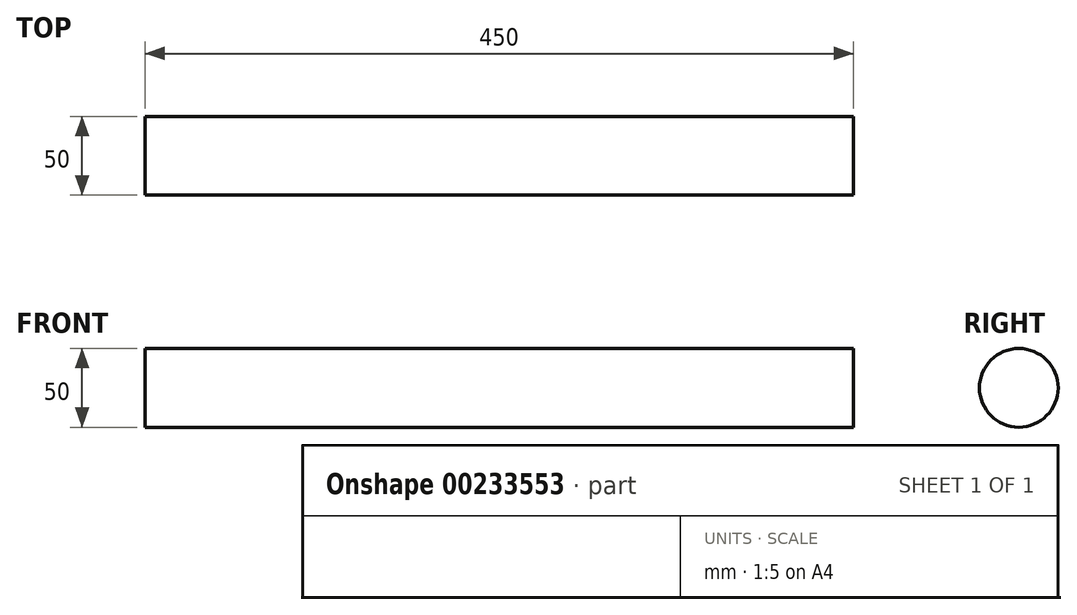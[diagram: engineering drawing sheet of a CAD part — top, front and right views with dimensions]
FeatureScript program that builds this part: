
annotation { "Feature Type Name" : "Feature", "Feature Type Description" : "" }
export const myFeature = defineFeature(function(context is Context, id is Id, definition is map)
    precondition{}
    {
        {
            var Q0;
            Q0=qCreatedBy(makeId("Front.planeOp"),FACE);
            var sketch = newSketch(context, id + "F0", { "sketchPlane" : qUnion([Q0])});
            skLineSegment(sketch, "E0.bottom", {"start": v(0, 0) * mm, "end": v(450, 0) * mm});
            skLineSegment(sketch, "E0.top", {"start": v(0, 25) * mm, "end": v(450, 25) * mm});
            skLineSegment(sketch, "E0.left", {"start": v(0, 0) * mm, "end": v(0, 25) * mm});
            skLineSegment(sketch, "E0.right", {"start": v(450, 0) * mm, "end": v(450, 25) * mm});
            skSolve(sketch);
        }
        {
            var Q0;
            Q0=makeQuery(id+"F0.imprint","IMPRINT",FACE,{"disambiguationData":[TD([[makeQuery(id+"F0.imprint","IMPRINT",EDGE,{"derivedFrom":sQuery(id+"F0.wireOp",EDGE,"E0.bottom")}),1.0]])]});
            var Q1;
            Q1=sQuery(id+"F0.wireOp",EDGE,"E0.bottom");
            revolve(context, id + "F1", {"entities" : qUnion([Q0]), "axis" : qUnion([Q1]), "revolveType" : RevolveType.FULL});
        }
    });
